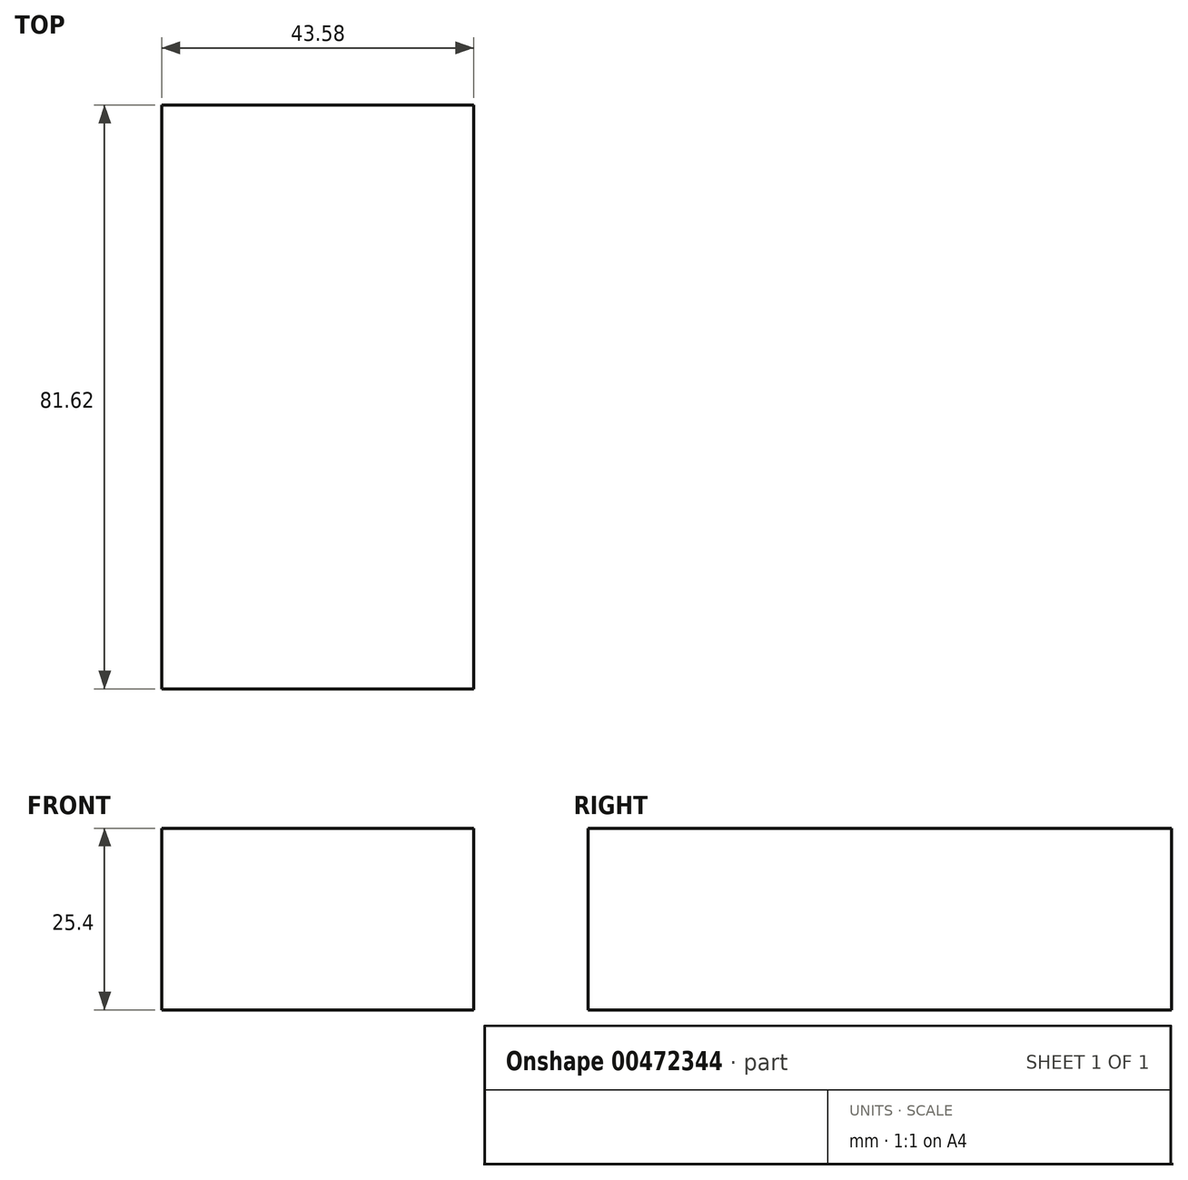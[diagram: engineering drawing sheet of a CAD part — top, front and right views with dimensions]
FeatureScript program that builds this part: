
annotation { "Feature Type Name" : "Feature", "Feature Type Description" : "" }
export const myFeature = defineFeature(function(context is Context, id is Id, definition is map)
    precondition{}
    {
        {
            var Q0;
            Q0=qCreatedBy(makeId("Top.planeOp"),FACE);
            var sketch = newSketch(context, id + "F0", { "sketchPlane" : qUnion([Q0])});
            skLineSegment(sketch, "E0", {"start": v(0, 40.33) * mm, "end": v(43.58, 40.33) * mm});
            skLineSegment(sketch, "E1", {"start": v(43.58, 40.33) * mm, "end": v(43.58, -41.3) * mm});
            skLineSegment(sketch, "E2", {"start": v(43.58, -41.3) * mm, "end": v(0, -41.3) * mm});
            skLineSegment(sketch, "E3", {"start": v(0, -41.3) * mm, "end": v(0, 40.33) * mm});
            skSolve(sketch);
        }
        {
            var Q0;
            Q0 = qSketchRegion(id + "F0", true);
            extrude(context, id + "F1", {"entities" : qUnion([Q0]), "depth" : 25.4 * mm});
        }
    });
